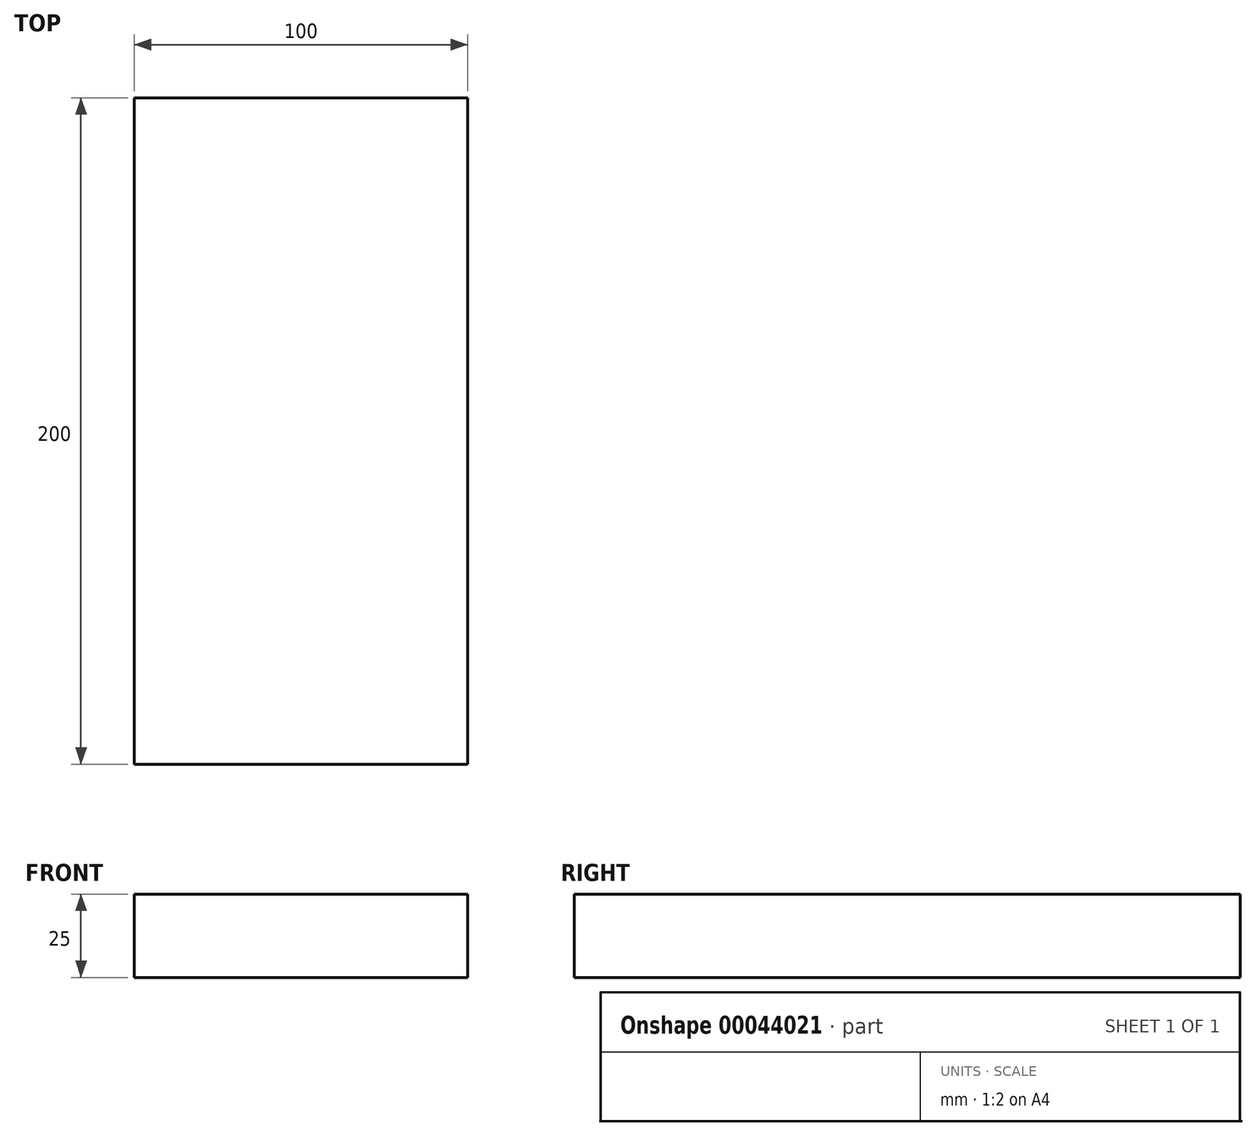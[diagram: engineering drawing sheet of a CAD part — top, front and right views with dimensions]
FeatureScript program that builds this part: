
annotation { "Feature Type Name" : "Feature", "Feature Type Description" : "" }
export const myFeature = defineFeature(function(context is Context, id is Id, definition is map)
    precondition{}
    {
        {
            var Q0;
            Q0=qCreatedBy(makeId("Top.planeOp"),FACE);
            var sketch = newSketch(context, id + "F0", { "sketchPlane" : qUnion([Q0])});
            skLineSegment(sketch, "E0.bottom", {"start": v(-50, -50) * mm, "end": v(50, -50) * mm});
            skLineSegment(sketch, "E0.top", {"start": v(-50, 150) * mm, "end": v(50, 150) * mm});
            skLineSegment(sketch, "E0.left", {"start": v(-50, -50) * mm, "end": v(-50, 150) * mm});
            skLineSegment(sketch, "E0.right", {"start": v(50, -50) * mm, "end": v(50, 150) * mm});
            skPoint(sketch, "E1.left.start.orphan", {"position": v(0, 150) * mm});
            skSolve(sketch);
        }
        {
            var Q0;
            Q0=makeQuery(id+"F0.imprint","IMPRINT",FACE,{"disambiguationData":[TD([[makeQuery(id+"F0.imprint","IMPRINT",EDGE,{"derivedFrom":sQuery(id+"F0.wireOp",EDGE,"E0.bottom")}),1.0]])]});
            extrude(context, id + "F1", {"entities" : qUnion([Q0]), "depth" : 25 * mm});
        }
    });
